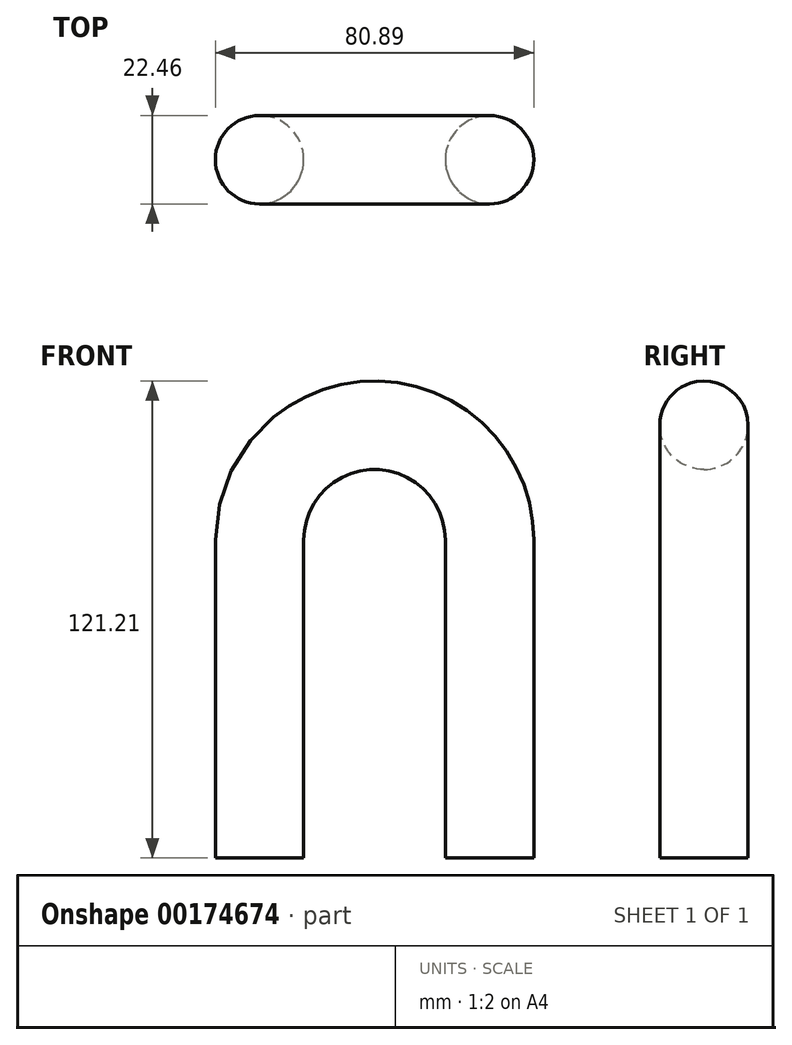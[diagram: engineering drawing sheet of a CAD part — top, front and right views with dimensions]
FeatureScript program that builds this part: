
annotation { "Feature Type Name" : "Feature", "Feature Type Description" : "" }
export const myFeature = defineFeature(function(context is Context, id is Id, definition is map)
    precondition{}
    {
        {
            var Q0;
            Q0=qCreatedBy(makeId("Front.planeOp"),FACE);
            var sketch = newSketch(context, id + "F0", { "sketchPlane" : qUnion([Q0])});
            skLineSegment(sketch, "E0.bottom", {"start": v(-26.08, 43.38) * mm, "end": v(-26.08, 43.38) * mm});
            skLineSegment(sketch, "E0.left", {"start": v(-26.08, 43.38) * mm, "end": v(-26.08, -37.38) * mm});
            skLineSegment(sketch, "E0.right", {"start": v(32.35, 43.38) * mm, "end": v(32.35, -37.38) * mm});
            skArc(sketch, "E1", {"start": v(32.35, 43.38) * mm, "mid": v(3.14, 72.6) * mm, "end": v(-26.08, 43.38) * mm});
            skLineSegment(sketch, "E2.trimOffspring", {"start": v(32.35, 43.38) * mm, "end": v(32.35, 43.38) * mm});
            skSolve(sketch);
        }
        {
            var Q0;
            Q0=qCreatedBy(makeId("Top.planeOp"),FACE);
            var sketch = newSketch(context, id + "F1", { "sketchPlane" : qUnion([Q0])});
            skCircle(sketch, "E3", {"center": v(-26.08, 0) * mm, "radius": 11.23 * mm});
            skSolve(sketch);
        }
        {
            var Q0;
            Q0=makeQuery(id+"F1.imprint","IMPRINT",FACE,{"disambiguationData":[TD([[makeQuery(id+"F1.imprint","IMPRINT",EDGE,{"derivedFrom":sQuery(id+"F1.wireOp",EDGE,"E3")}),1.0]])]});
            var Q1;
            Q1=sQuery(id+"F0.wireOp",EDGE,"E0.left");
            var Q2;
            Q2=sQuery(id+"F0.wireOp",EDGE,"E1");
            var Q3;
            Q3=sQuery(id+"F0.wireOp",EDGE,"E0.right");
            sweep(context, id + "F2", {"profiles" : qUnion([Q0]), "path" : qUnion([Q1, Q2, Q3])});
        }
    });
